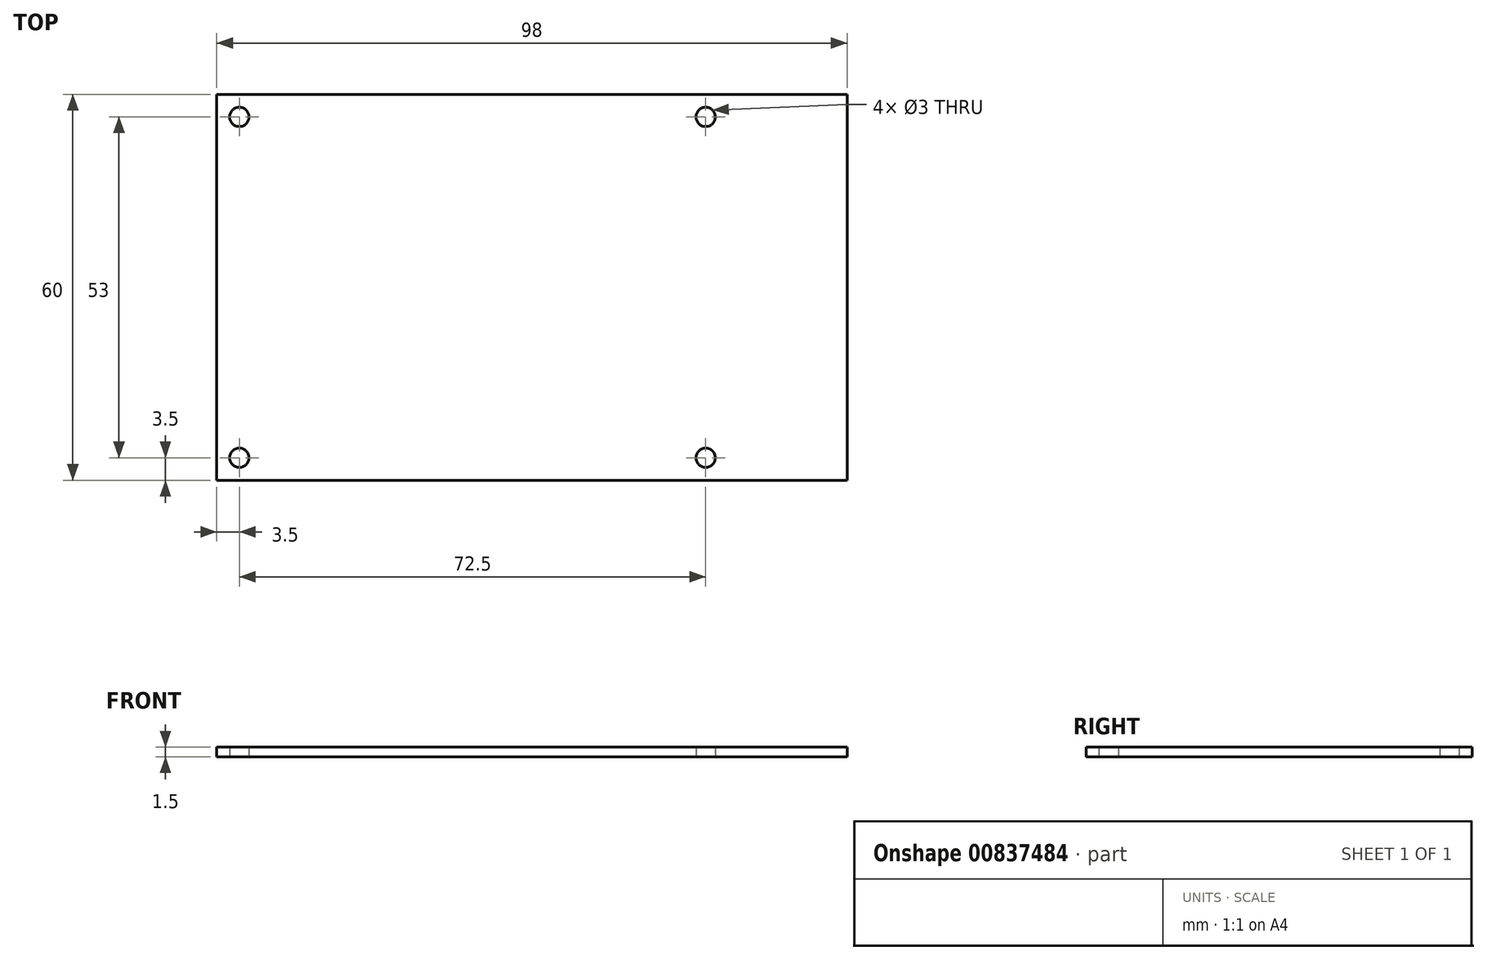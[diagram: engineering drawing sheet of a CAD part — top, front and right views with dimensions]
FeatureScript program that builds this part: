
annotation { "Feature Type Name" : "Feature", "Feature Type Description" : "" }
export const myFeature = defineFeature(function(context is Context, id is Id, definition is map)
    precondition{}
    {
        {
            var Q0;
            Q0=qCreatedBy(makeId("Top.planeOp"),FACE);
            var sketch = newSketch(context, id + "F0", { "sketchPlane" : qUnion([Q0])});
            skLineSegment(sketch, "E0.bottom", {"start": v(49, -30) * mm, "end": v(-49, -30) * mm});
            skLineSegment(sketch, "E0.top", {"start": v(49, 30) * mm, "end": v(-49, 30) * mm});
            skLineSegment(sketch, "E0.left", {"start": v(49, -30) * mm, "end": v(49, 30) * mm});
            skLineSegment(sketch, "E0.right", {"start": v(-49, -30) * mm, "end": v(-49, 30) * mm});
            skPoint(sketch, "E1.middle", {"position": v(0, 0) * mm});
            skCircle(sketch, "E2", {"center": v(27, 26.5) * mm, "radius": 1.5 * mm});
            skCircle(sketch, "E3", {"center": v(27, -26.5) * mm, "radius": 1.5 * mm});
            skCircle(sketch, "E4", {"center": v(-45.5, -26.5) * mm, "radius": 1.5 * mm});
            skCircle(sketch, "E5", {"center": v(-45.5, 26.5) * mm, "radius": 1.5 * mm});
            skLineSegment(sketch, "E6.bottom", {"start": v(27, -26.5) * mm, "end": v(-45.5, -26.5) * mm, "construction": true});
            skLineSegment(sketch, "E6.top", {"start": v(27, 26.5) * mm, "end": v(-45.5, 26.5) * mm, "construction": true});
            skLineSegment(sketch, "E6.left", {"start": v(27, -26.5) * mm, "end": v(27, 26.5) * mm, "construction": true});
            skLineSegment(sketch, "E6.right", {"start": v(-45.5, -26.5) * mm, "end": v(-45.5, 26.5) * mm, "construction": true});
            skPoint(sketch, "E6.middle", {"position": v(-9.25, 0) * mm});
            skLineSegment(sketch, "E7", {"start": v(-45.5, 26.5) * mm, "end": v(-45.5, 30) * mm, "construction": true});
            skLineSegment(sketch, "E8", {"start": v(-45.5, 26.5) * mm, "end": v(-49, 26.5) * mm, "construction": true});
            skSolve(sketch);
        }
        {
            var Q0;
            Q0=qSketchRegion(id+"F0",true);
            extrude(context, id + "F1", {"entities" : qUnion([Q0]), "depth" : 1.5 * mm, "offsetDistance" : 25 * mm});
        }
    });
